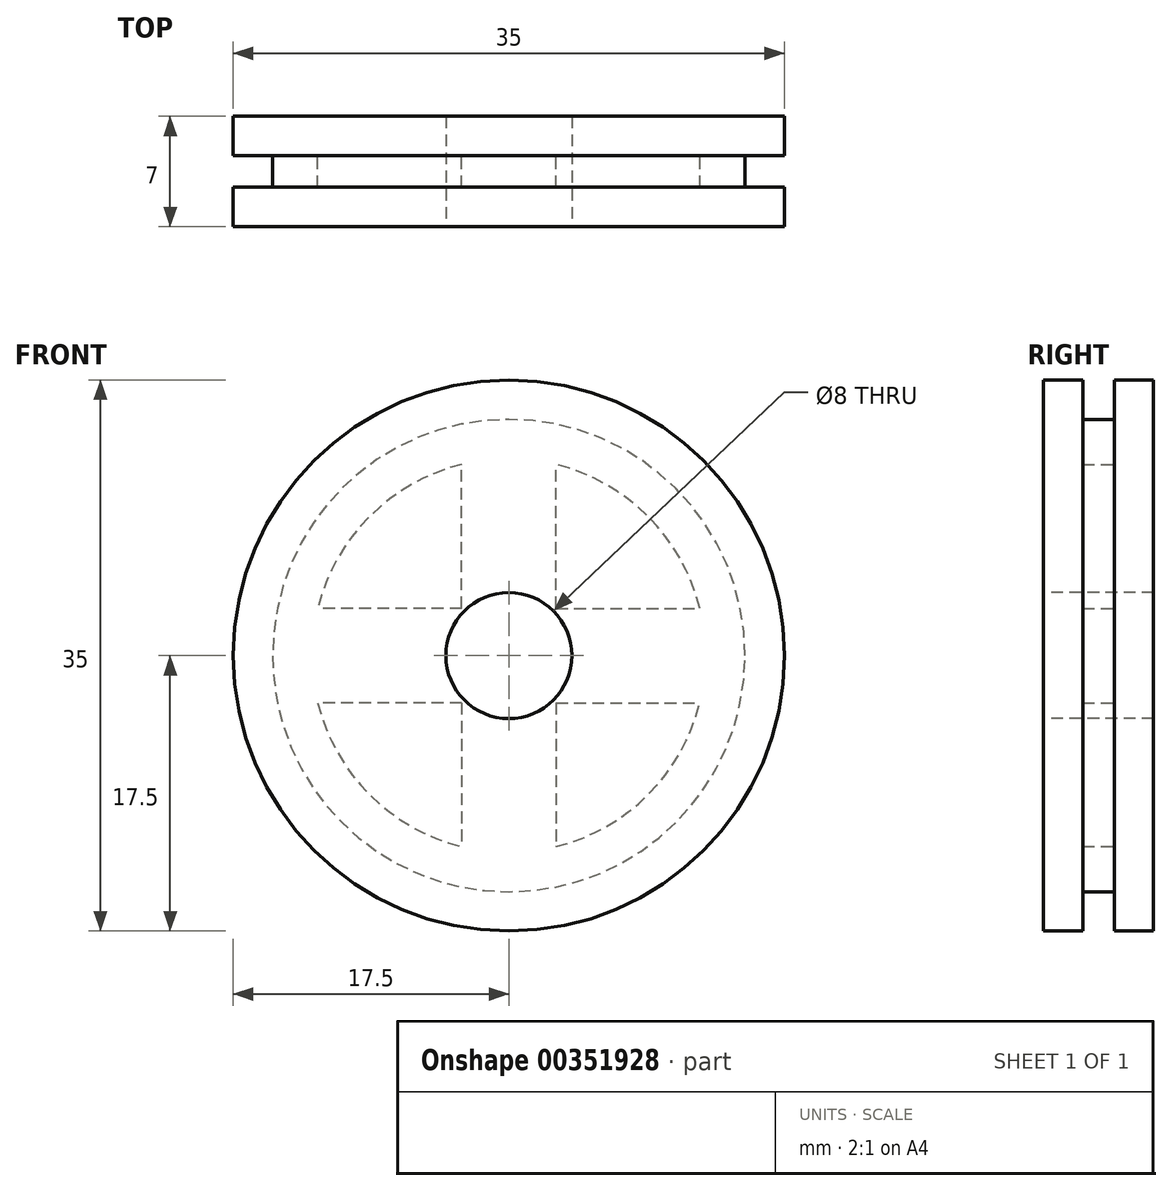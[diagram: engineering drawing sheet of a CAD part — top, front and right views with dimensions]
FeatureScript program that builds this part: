
annotation { "Feature Type Name" : "Feature", "Feature Type Description" : "" }
export const myFeature = defineFeature(function(context is Context, id is Id, definition is map)
    precondition{}
    {
        {
            var Q0;
            Q0=qCreatedBy(makeId("Front.planeOp"),FACE);
            var sketch = newSketch(context, id + "F0", { "sketchPlane" : qUnion([Q0])});
            skCircle(sketch, "E0", {"center": v(0, 0) * mm, "radius": 15 * mm});
            skArc(sketch, "E1", {"start": v(-3, 12.13) * mm, "mid": v(-8.84, 8.84) * mm, "end": v(-12.13, 3) * mm});
            skLineSegment(sketch, "E2", {"start": v(3, 3) * mm, "end": v(3, 12.13) * mm});
            skLineSegment(sketch, "E3", {"start": v(3, -3) * mm, "end": v(3, -12.13) * mm});
            skLineSegment(sketch, "E4", {"start": v(-3, 3) * mm, "end": v(-3, 12.13) * mm});
            skLineSegment(sketch, "E5", {"start": v(-3, -3) * mm, "end": v(-3, -12.13) * mm});
            skLineSegment(sketch, "E6", {"start": v(3, -3) * mm, "end": v(12.13, -3) * mm});
            skLineSegment(sketch, "E7", {"start": v(-3, -3) * mm, "end": v(-12.13, -3) * mm});
            skLineSegment(sketch, "E8", {"start": v(3, 3) * mm, "end": v(12.13, 3) * mm});
            skLineSegment(sketch, "E9", {"start": v(-3, 3) * mm, "end": v(-12.13, 3) * mm});
            skArc(sketch, "E10.trimOffspring", {"start": v(-12.13, -3) * mm, "mid": v(0, -12.5) * mm, "end": v(12.13, -3) * mm});
            skArc(sketch, "E11.trimOffspring", {"start": v(12.13, 3) * mm, "mid": v(8.84, 8.84) * mm, "end": v(3, 12.13) * mm});
            skSolve(sketch);
        }
        {
            var Q0;
            Q0 = qSketchRegion(id + "F0", true);
            extrude(context, id + "F1", {"entities" : qUnion([Q0]), "depth" : 2 * mm});
        }
        {
            var Q0;
            Q0=makeQuery(id+"F1.opExtrude","CAP_FACE",FACE,{"disambiguationData":[OSD([sQuery(id+"F0.wireOp",EDGE,"E0"),sQuery(id+"F0.wireOp",EDGE,"E1"),sQuery(id+"F0.wireOp",EDGE,"E2"),sQuery(id+"F0.wireOp",EDGE,"E3"),sQuery(id+"F0.wireOp",EDGE,"E4"),sQuery(id+"F0.wireOp",EDGE,"E5"),sQuery(id+"F0.wireOp",EDGE,"E6"),sQuery(id+"F0.wireOp",EDGE,"E7"),sQuery(id+"F0.wireOp",EDGE,"E8"),sQuery(id+"F0.wireOp",EDGE,"E9"),sQuery(id+"F0.wireOp",EDGE,"E10.trimOffspring"),sQuery(id+"F0.wireOp",EDGE,"E11.trimOffspring")])],"isStart":true});
            var sketch = newSketch(context, id + "F2", { "sketchPlane" : qUnion([Q0])});
            skCircle(sketch, "E12", {"center": v(0, 0) * mm, "radius": 17.5 * mm});
            skSolve(sketch);
        }
        {
            var Q0;
            Q0 = qSketchRegion(id + "F2", true);
            extrude(context, id + "F3", {"entities" : qUnion([Q0]), "operationType" : NewBodyOperationType.ADD, "depth" : 2.5 * mm});
        }
        {
            var Q0;
            Q0=makeQuery(id+"F1.opExtrude","CAP_FACE",FACE,{"disambiguationData":[OSD([sQuery(id+"F0.wireOp",EDGE,"E0"),sQuery(id+"F0.wireOp",EDGE,"E1"),sQuery(id+"F0.wireOp",EDGE,"E2"),sQuery(id+"F0.wireOp",EDGE,"E3"),sQuery(id+"F0.wireOp",EDGE,"E4"),sQuery(id+"F0.wireOp",EDGE,"E5"),sQuery(id+"F0.wireOp",EDGE,"E6"),sQuery(id+"F0.wireOp",EDGE,"E7"),sQuery(id+"F0.wireOp",EDGE,"E8"),sQuery(id+"F0.wireOp",EDGE,"E9"),sQuery(id+"F0.wireOp",EDGE,"E10.trimOffspring"),sQuery(id+"F0.wireOp",EDGE,"E11.trimOffspring")])],"isStart":false});
            var sketch = newSketch(context, id + "F4", { "sketchPlane" : qUnion([Q0])});
            skCircle(sketch, "E13", {"center": v(0, 0) * mm, "radius": 17.5 * mm});
            skSolve(sketch);
        }
        {
            var Q0;
            Q0 = qSketchRegion(id + "F4", true);
            extrude(context, id + "F5", {"entities" : qUnion([Q0]), "operationType" : NewBodyOperationType.ADD, "depth" : 2.5 * mm});
        }
        {
            var Q0;
            Q0=makeQuery(id+"F5.opExtrude","CAP_FACE",FACE,{"disambiguationData":[OSD([sQuery(id+"F4.wireOp",EDGE,"E13")])],"isStart":false});
            var sketch = newSketch(context, id + "F6", { "sketchPlane" : qUnion([Q0])});
            skPoint(sketch, "E14", {"position": v(0, 0) * mm});
            skSolve(sketch);
        }
        {
            var Q0;
            Q0=sQuery(id+"F6.wireOp",VERTEX,"E14");
            var Q1;
            Q1=makeQuery(id+"F1.opExtrude","SWEPT_BODY",BODY,{"disambiguationData":[OSD([sQuery(id+"F0.wireOp",EDGE,"E0"),sQuery(id+"F0.wireOp",EDGE,"E1"),sQuery(id+"F0.wireOp",EDGE,"E2"),sQuery(id+"F0.wireOp",EDGE,"E3"),sQuery(id+"F0.wireOp",EDGE,"E4"),sQuery(id+"F0.wireOp",EDGE,"E5"),sQuery(id+"F0.wireOp",EDGE,"E6"),sQuery(id+"F0.wireOp",EDGE,"E7"),sQuery(id+"F0.wireOp",EDGE,"E8"),sQuery(id+"F0.wireOp",EDGE,"E9"),sQuery(id+"F0.wireOp",EDGE,"E10.trimOffspring"),sQuery(id+"F0.wireOp",EDGE,"E11.trimOffspring")])]});
            hole(context, id + "F7", {"style" : HoleStyle.SIMPLE, "endStyle" : HoleEndStyle.THROUGH, "holeDiameter" : 8 * mm, "isTappedThrough" : true, "tappedDepth" : 12 * mm, "tapClearance" : 3, "locations" : qUnion([Q0]), "scope" : qUnion([Q1])});
        }
    });
